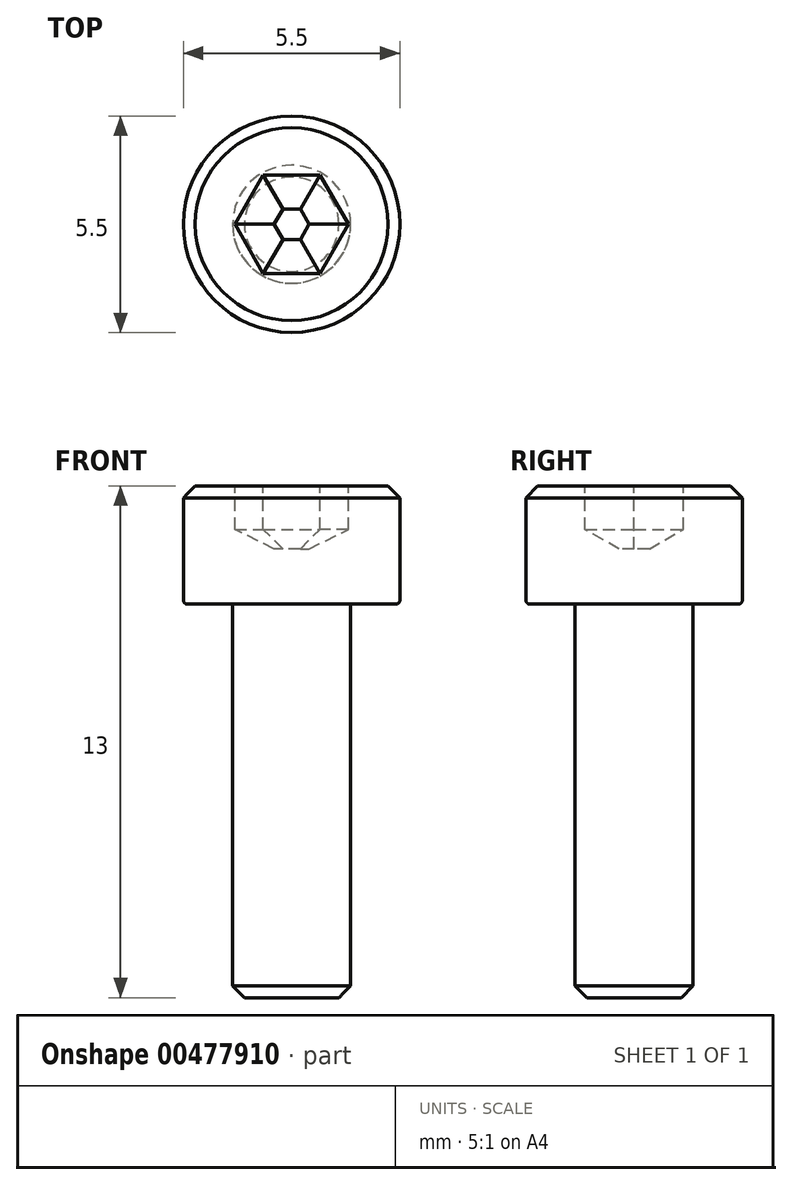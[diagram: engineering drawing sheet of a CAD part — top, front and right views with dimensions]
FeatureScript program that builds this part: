
annotation { "Feature Type Name" : "Feature", "Feature Type Description" : "" }
export const myFeature = defineFeature(function(context is Context, id is Id, definition is map)
    precondition{}
    {
        {
            var Q0;
            Q0=qCreatedBy(makeId("Front.planeOp"),FACE);
            var sketch = newSketch(context, id + "F0", { "sketchPlane" : qUnion([Q0])});
            skLineSegment(sketch, "E0", {"start": v(0, 0) * mm, "end": v(0, -13.37) * mm, "construction": true});
            skLineSegment(sketch, "E1", {"start": v(0, 0) * mm, "end": v(2.75, 0) * mm});
            skLineSegment(sketch, "E2", {"start": v(2.75, 0) * mm, "end": v(2.75, -3) * mm});
            skLineSegment(sketch, "E3", {"start": v(2.75, -3) * mm, "end": v(1.5, -3) * mm});
            skLineSegment(sketch, "E4", {"start": v(1.5, -3) * mm, "end": v(1.5, -13) * mm});
            skLineSegment(sketch, "E5", {"start": v(1.5, -13) * mm, "end": v(0, -13) * mm});
            skLineSegment(sketch, "E6", {"start": v(0, -13) * mm, "end": v(0, 0) * mm});
            skSolve(sketch);
        }
        {
            var Q0;
            Q0=qSketchRegion(id+"F0",true);
            var Q1;
            Q1=sQuery(id+"F0.wireOp",EDGE,"E6");
            revolve(context, id + "F1", {"entities" : qUnion([Q0]), "axis" : qUnion([Q1]), "revolveType" : RevolveType.FULL});
        }
        {
            var Q0;
            Q0=makeQuery(id+"F1.opRevolve","SWEPT_FACE",FACE,{"disambiguationData":[OSD([sQuery(id+"F0.wireOp",EDGE,"E1")])]});
            var sketch = newSketch(context, id + "F2", { "sketchPlane" : qUnion([Q0])});
            skCircle(sketch, "E7.cCircle", {"center": v(0, 0) * mm, "radius": 1.25 * mm, "construction": true});
            skLineSegment(sketch, "E7.0", {"start": v(-0.72, 1.25) * mm, "end": v(0.72, 1.25) * mm});
            skLineSegment(sketch, "E7.1", {"start": v(0.72, 1.25) * mm, "end": v(1.44, 0) * mm});
            skLineSegment(sketch, "E7.2", {"start": v(1.44, 0) * mm, "end": v(0.72, -1.25) * mm});
            skLineSegment(sketch, "E7.3", {"start": v(0.72, -1.25) * mm, "end": v(-0.72, -1.25) * mm});
            skLineSegment(sketch, "E7.4", {"start": v(-0.72, -1.25) * mm, "end": v(-1.44, 0) * mm});
            skLineSegment(sketch, "E7.5", {"start": v(-1.44, 0) * mm, "end": v(-0.72, 1.25) * mm});
            skPoint(sketch, "E7.0.midPoint", {"position": v(0, 1.25) * mm});
            skSolve(sketch);
        }
        {
            var Q0;
            Q0=makeQuery(id+"F2.imprint","IMPRINT",FACE,{"disambiguationData":[TD([[makeQuery(id+"F2.imprint","IMPRINT",EDGE,{"derivedFrom":sQuery(id+"F2.wireOp",EDGE,"E7.0")}),-1.0]])]});
            extrude(context, id + "F3", {"entities" : qUnion([Q0]), "operationType" : NewBodyOperationType.REMOVE, "oppositeDirection" : true, "depth" : 1.6 * mm});
        }
        {
            var Q0;
            Q0=makeQuery(id+"F3.boolean.opBoolean","COPY",FACE,{"derivedFrom":makeQuery(id+"F3.opExtrude","CAP_FACE",FACE,{"disambiguationData":[OSD([sQuery(id+"F2.wireOp",EDGE,"E7.0"),sQuery(id+"F2.wireOp",EDGE,"E7.1"),sQuery(id+"F2.wireOp",EDGE,"E7.2"),sQuery(id+"F2.wireOp",EDGE,"E7.3"),sQuery(id+"F2.wireOp",EDGE,"E7.4"),sQuery(id+"F2.wireOp",EDGE,"E7.5")])],"isStart":false})});
            chamfer(context, id + "F4", {"entities" : qUnion([Q0]), "chamferType" : ChamferType.OFFSET_ANGLE, "width" : .5 * mm, "oppositeDirection" : false, "angle" : 60 * degree, "tangentPropagation" : true});
        }
        {
            var Q0;
            Q0=makeQuery(id+"F1.opRevolve","SWEPT_EDGE",EDGE,{"disambiguationData":[OSD([sQuery(id+"F0.wireOp",EDGE,"E1"),sQuery(id+"F0.wireOp",EDGE,"E2")])]});
            var Q1;
            Q1=makeQuery(id+"F1.opRevolve","SWEPT_EDGE",EDGE,{"disambiguationData":[OSD([sQuery(id+"F0.wireOp",EDGE,"E4"),sQuery(id+"F0.wireOp",EDGE,"E5")])]});
            chamfer(context, id + "F5", {"entities" : qUnion([Q0, Q1]), "width" : .3 * mm, "tangentPropagation" : true});
        }
        {
            var Q0;
            Q0=makeQuery(id+"F1.opRevolve","SWEPT_EDGE",EDGE,{"disambiguationData":[OSD([sQuery(id+"F0.wireOp",EDGE,"E2"),sQuery(id+"F0.wireOp",EDGE,"E3")])]});
            fillet(context, id + "F6", {"entities" : qUnion([Q0]), "radius" : .1 * mm, "tangentPropagation" : true, "allowEdgeOverflow" : false});
        }
        {
            var Q0;
            Q0=makeQuery(id+"F1.opRevolve","SWEPT_BODY",BODY,{"disambiguationData":[OSD([sQuery(id+"F0.wireOp",EDGE,"E1"),sQuery(id+"F0.wireOp",EDGE,"E2"),sQuery(id+"F0.wireOp",EDGE,"E3"),sQuery(id+"F0.wireOp",EDGE,"E4"),sQuery(id+"F0.wireOp",EDGE,"E5"),sQuery(id+"F0.wireOp",EDGE,"E6")])]});
            transform(context, id + "F7", {"entities" : qUnion([Q0]), "transformType" : TransformType.COPY});
        }
        {
            var Q0;
            Q0=makeQuery(id+"F7.opPattern","COPY",BODY,{"derivedFrom":makeQuery(id+"F1.opRevolve","SWEPT_BODY",BODY,{"disambiguationData":[OSD([sQuery(id+"F0.wireOp",EDGE,"E1"),sQuery(id+"F0.wireOp",EDGE,"E2"),sQuery(id+"F0.wireOp",EDGE,"E3"),sQuery(id+"F0.wireOp",EDGE,"E4"),sQuery(id+"F0.wireOp",EDGE,"E5"),sQuery(id+"F0.wireOp",EDGE,"E6")])]}),"instanceName":"1"});
            deleteBodies(context, id + "F8", {"entities" : qUnion([Q0])});
        }
    });
